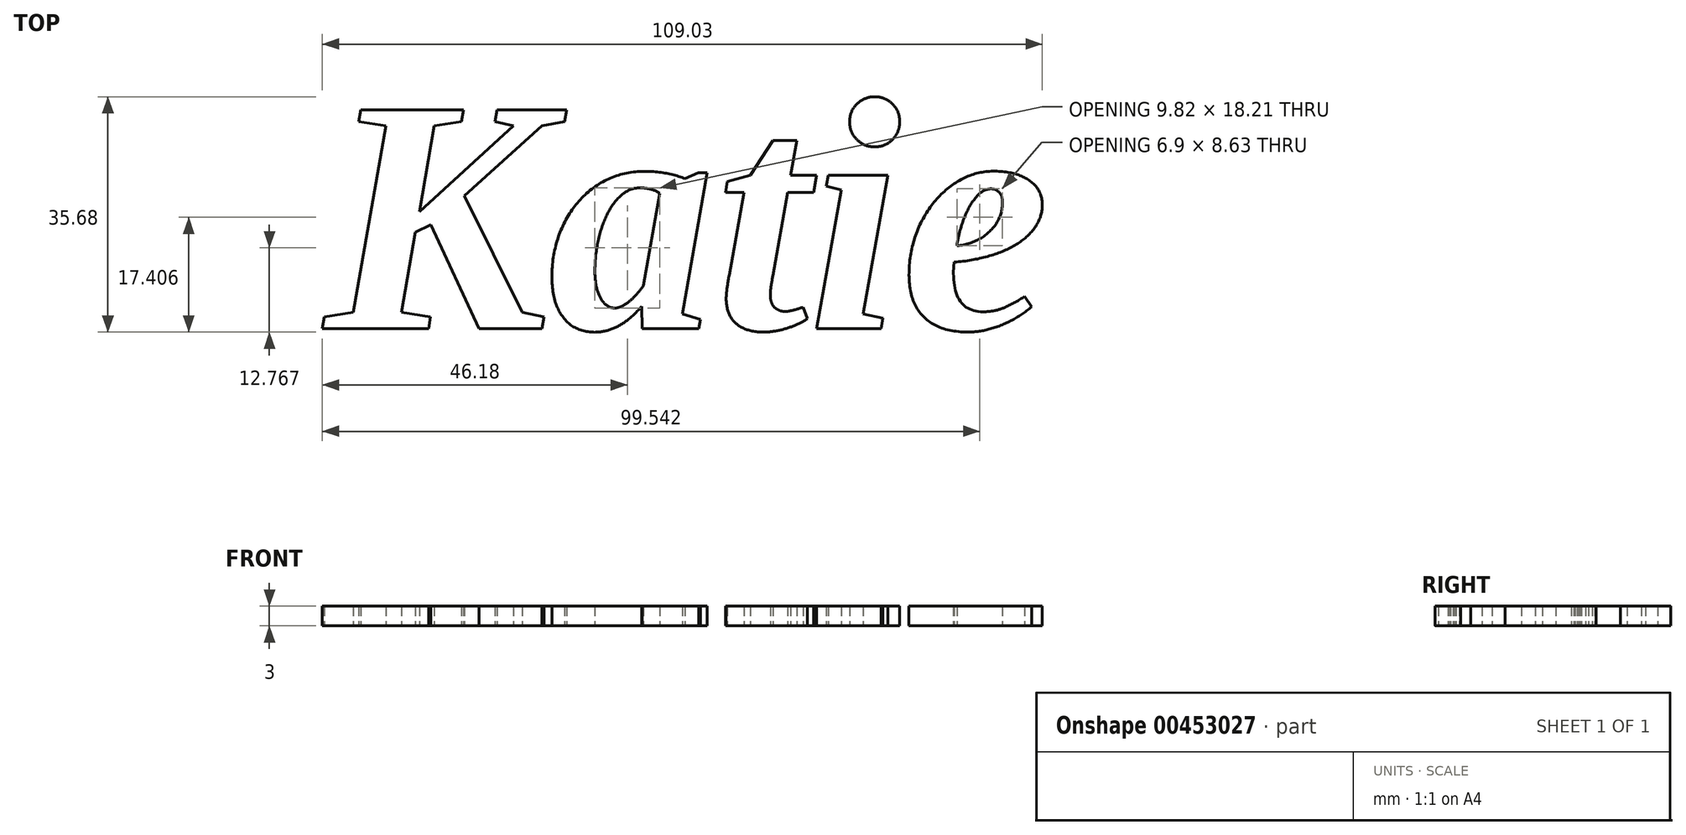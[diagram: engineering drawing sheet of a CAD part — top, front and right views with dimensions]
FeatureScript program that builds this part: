
annotation { "Feature Type Name" : "Feature", "Feature Type Description" : "" }
export const myFeature = defineFeature(function(context is Context, id is Id, definition is map)
    precondition{}
    {
        {
            var Q0;
            Q0=qCreatedBy(makeId("Top.planeOp"),FACE);
            var sketch = newSketch(context, id + "F0", { "sketchPlane" : qUnion([Q0])});
            skText(sketch, "E0", { "text": "Katie", "fontName": "Tinos-BoldItalic.ttf"});
            const initialGuessF0  = {"E0": [-0.05581, 0.0067, 1, 0, 0.03648]};
            skSetInitialGuess(sketch, initialGuessF0);
            skSolve(sketch);
        }
        {
            var Q0;
            Q0 = qSketchRegion(id + "F0", true);
            extrude(context, id + "F1", {"entities" : qUnion([Q0]), "depth" : 3 * mm});
        }
    });
